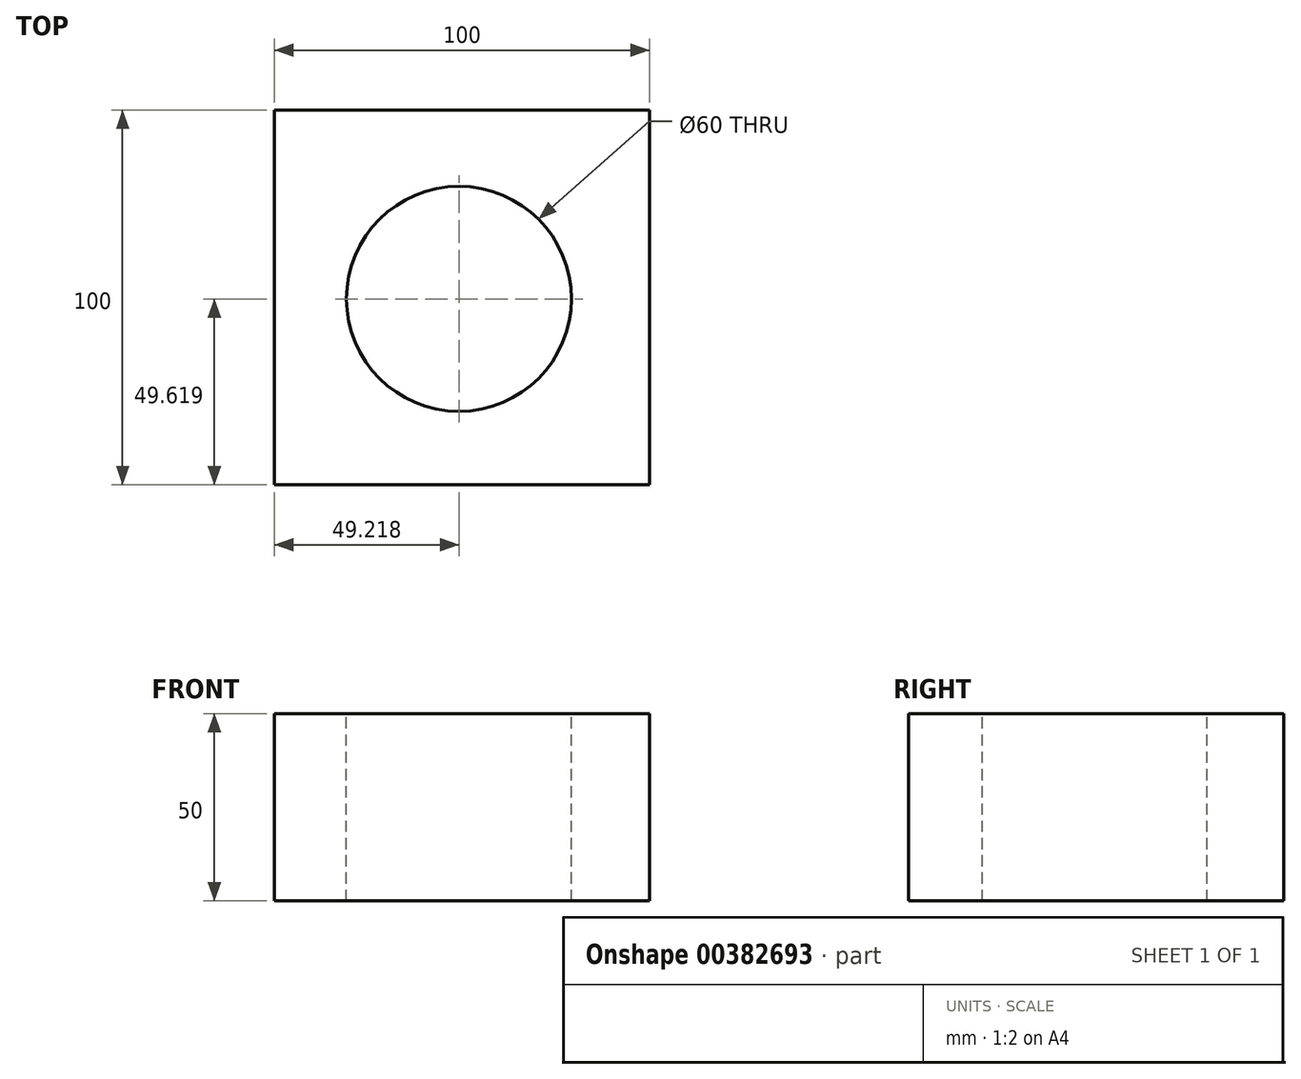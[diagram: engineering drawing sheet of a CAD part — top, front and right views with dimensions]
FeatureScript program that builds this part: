
annotation { "Feature Type Name" : "Feature", "Feature Type Description" : "" }
export const myFeature = defineFeature(function(context is Context, id is Id, definition is map)
    precondition{}
    {
        {
            var Q0;
            Q0=qCreatedBy(makeId("Top.planeOp"),FACE);
            var sketch = newSketch(context, id + "F0", { "sketchPlane" : qUnion([Q0])});
            skLineSegment(sketch, "E0.bottom", {"start": v(0, 0) * mm, "end": v(100, 0) * mm});
            skLineSegment(sketch, "E0.top", {"start": v(0, 100) * mm, "end": v(100, 100) * mm});
            skLineSegment(sketch, "E0.left", {"start": v(0, 0) * mm, "end": v(0, 100) * mm});
            skLineSegment(sketch, "E0.right", {"start": v(100, 0) * mm, "end": v(100, 100) * mm});
            skSolve(sketch);
        }
        {
            var Q0;
            Q0=makeQuery(id+"F0.imprint","IMPRINT",FACE,{"disambiguationData":[TD([[makeQuery(id+"F0.imprint","IMPRINT",EDGE,{"derivedFrom":sQuery(id+"F0.wireOp",EDGE,"E0.bottom")}),1.0]])]});
            extrude(context, id + "F1", {"entities" : qUnion([Q0]), "depth" : 50 * mm});
        }
        {
            var Q0;
            Q0=makeQuery(id+"F1.opExtrude","CAP_FACE",FACE,{"disambiguationData":[OSD([sQuery(id+"F0.wireOp",EDGE,"E0.bottom"),sQuery(id+"F0.wireOp",EDGE,"E0.top"),sQuery(id+"F0.wireOp",EDGE,"E0.left"),sQuery(id+"F0.wireOp",EDGE,"E0.right")])],"isStart":false});
            var sketch = newSketch(context, id + "F2", { "sketchPlane" : qUnion([Q0])});
            skCircle(sketch, "E1", {"center": v(49.22, 49.62) * mm, "radius": 30 * mm});
            skSolve(sketch);
        }
        {
            var Q0;
            Q0 = qSketchRegion(id + "F2", true);
            extrude(context, id + "F3", {"entities" : qUnion([Q0]), "operationType" : NewBodyOperationType.REMOVE, "endBound" : BoundingType.THROUGH_ALL, "oppositeDirection" : true, "depth" : 25 * mm});
        }
    });
